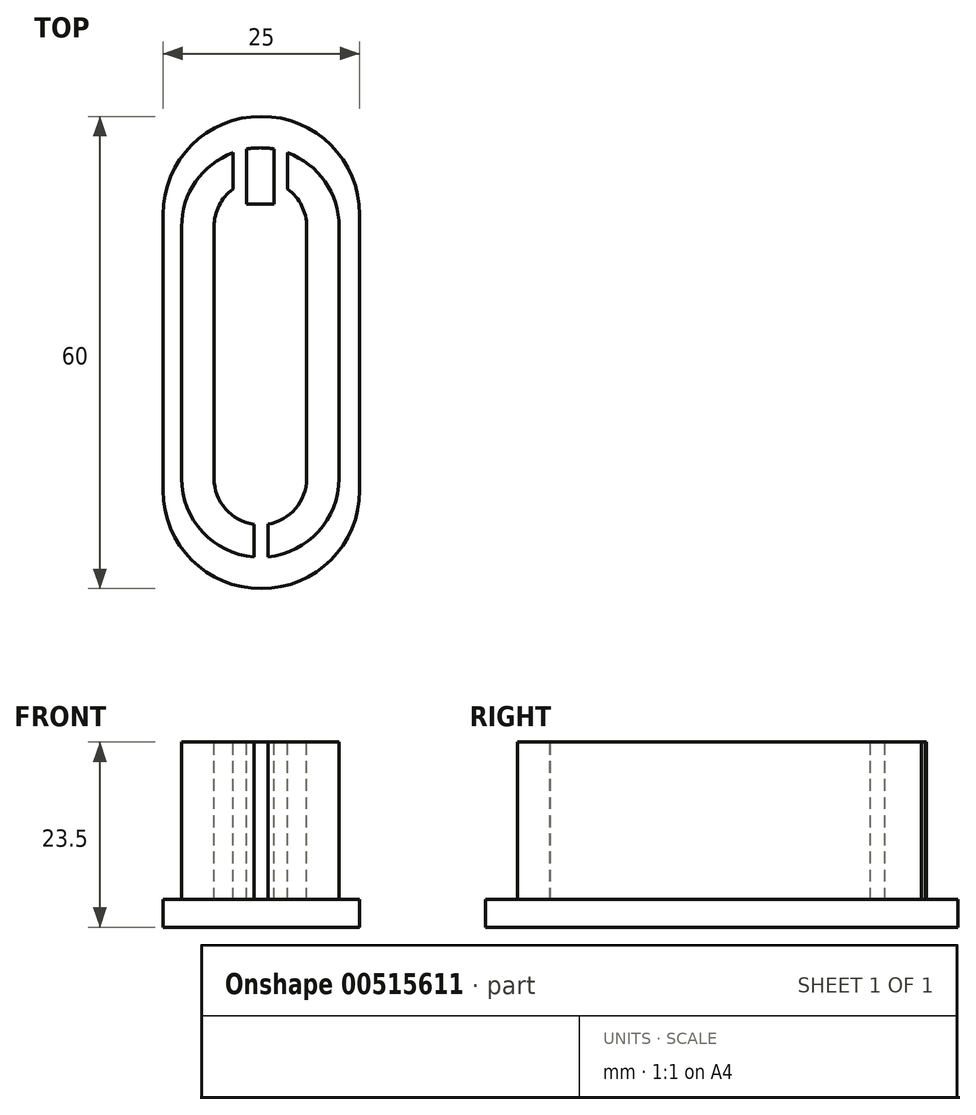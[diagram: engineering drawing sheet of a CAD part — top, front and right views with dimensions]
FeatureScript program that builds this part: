
annotation { "Feature Type Name" : "Feature", "Feature Type Description" : "" }
export const myFeature = defineFeature(function(context is Context, id is Id, definition is map)
    precondition{}
    {
        {
            var Q0;
            Q0=qCreatedBy(makeId("Top.planeOp"),FACE);
            var sketch = newSketch(context, id + "F0", { "sketchPlane" : qUnion([Q0])});
            skLineSegment(sketch, "E0", {"start": v(-12.5, 20) * mm, "end": v(-12.5, -15) * mm});
            skLineSegment(sketch, "E1", {"start": v(12.5, 20) * mm, "end": v(12.5, -15) * mm});
            skArc(sketch, "E2", {"start": v(12.5, 20) * mm, "mid": v(0, 32.5) * mm, "end": v(-12.5, 20) * mm});
            skArc(sketch, "E3", {"start": v(-12.5, -15) * mm, "mid": v(0, -27.5) * mm, "end": v(12.5, -15) * mm});
            skSolve(sketch);
        }
        {
            var Q0;
            Q0 = qSketchRegion(id + "F0", true);
            extrude(context, id + "F1", {"entities" : qUnion([Q0]), "depth" : 3.5 * mm, "offsetDistance" : 25 * mm});
        }
        {
            var Q0;
            Q0=makeQuery(id+"F1.opExtrude","CAP_FACE",FACE,{"disambiguationData":[OSD([sQuery(id+"F0.wireOp",EDGE,"E0"),sQuery(id+"F0.wireOp",EDGE,"E1"),sQuery(id+"F0.wireOp",EDGE,"E2"),sQuery(id+"F0.wireOp",EDGE,"E3")])],"isStart":false});
            var sketch = newSketch(context, id + "F2", { "sketchPlane" : qUnion([Q0])});
            skLineSegment(sketch, "E4.left", {"start": v(-10.13, 18.5) * mm, "end": v(-10.13, -13.5) * mm});
            skLineSegment(sketch, "E4.right", {"start": v(9.87, 18.5) * mm, "end": v(9.87, -13.5) * mm});
            skArc(sketch, "E5", {"start": v(-10.13, -13.5) * mm, "mid": v(-0.13, -23.5) * mm, "end": v(9.87, -13.5) * mm});
            skArc(sketch, "E6", {"start": v(9.87, 18.5) * mm, "mid": v(-0.13, 28.5) * mm, "end": v(-10.13, 18.5) * mm});
            skSolve(sketch);
        }
        {
            var Q0;
            Q0 = qSketchRegion(id + "F2", true);
            extrude(context, id + "F3", {"entities" : qUnion([Q0]), "operationType" : NewBodyOperationType.ADD, "depth" : 20 * mm, "offsetDistance" : 25 * mm});
        }
        {
            var Q0;
            Q0=makeQuery(id+"F3.opExtrude","CAP_FACE",FACE,{"disambiguationData":[OSD([sQuery(id+"F2.wireOp",EDGE,"E4.left"),sQuery(id+"F2.wireOp",EDGE,"E4.right"),sQuery(id+"F2.wireOp",EDGE,"E5"),sQuery(id+"F2.wireOp",EDGE,"E6")])],"isStart":false});
            var sketch = newSketch(context, id + "F4", { "sketchPlane" : qUnion([Q0])});
            skLineSegment(sketch, "E7.left", {"start": v(-6, 18.5) * mm, "end": v(-6, -13.5) * mm});
            skLineSegment(sketch, "E7.right", {"start": v(5.75, 18.5) * mm, "end": v(5.75, -13.5) * mm});
            skArc(sketch, "E8", {"start": v(5.75, 18.5) * mm, "mid": v(5.12, 21.16) * mm, "end": v(3.35, 23.24) * mm});
            skArc(sketch, "E9", {"start": v(-6, -13.5) * mm, "mid": v(-4.55, -17.37) * mm, "end": v(-0.9, -19.33) * mm});
            skLineSegment(sketch, "E10", {"start": v(-3.6, 23.24) * mm, "end": v(-3.6, 27.88) * mm});
            skLineSegment(sketch, "E11", {"start": v(-1.88, 16.66) * mm, "end": v(-1.88, 28.35) * mm});
            skLineSegment(sketch, "E12", {"start": v(1.62, 16.66) * mm, "end": v(1.62, 28.35) * mm});
            skLineSegment(sketch, "E13", {"start": v(3.35, 23.24) * mm, "end": v(3.35, 27.88) * mm});
            skArc(sketch, "E14.trimOffspring", {"start": v(-3.6, 23.24) * mm, "mid": v(-5.37, 21.16) * mm, "end": v(-6, 18.5) * mm});
            skArc(sketch, "E15", {"start": v(-1.88, 28.35) * mm, "mid": v(-2.82, 28.38) * mm, "end": v(-3.6, 27.88) * mm});
            skArc(sketch, "E16", {"start": v(3.35, 27.88) * mm, "mid": v(2.58, 28.47) * mm, "end": v(1.62, 28.35) * mm});
            skLineSegment(sketch, "E17", {"start": v(-0.9, -19.33) * mm, "end": v(-0.9, -23.47) * mm});
            skLineSegment(sketch, "E18", {"start": v(0.82, -19.3) * mm, "end": v(0.82, -23.45) * mm});
            skArc(sketch, "E19.trimOffspring", {"start": v(0.82, -19.3) * mm, "mid": v(4.35, -17.3) * mm, "end": v(5.75, -13.5) * mm});
            skArc(sketch, "E20", {"start": v(-0.9, -23.47) * mm, "mid": v(-0.04, -24.32) * mm, "end": v(0.82, -23.45) * mm});
            skLineSegment(sketch, "E21.top", {"start": v(-1.88, 21.35) * mm, "end": v(1.62, 21.35) * mm});
            skLineSegment(sketch, "E21.left", {"start": v(-1.88, 21.35) * mm, "end": v(-1.88, 16.66) * mm});
            skLineSegment(sketch, "E21.right", {"start": v(1.62, 21.35) * mm, "end": v(1.62, 16.66) * mm});
            skSolve(sketch);
        }
        {
            var Q0;
            Q0 = qSketchRegion(id + "F4", true);
            extrude(context, id + "F5", {"entities" : qUnion([Q0]), "operationType" : NewBodyOperationType.REMOVE, "oppositeDirection" : true, "depth" : 20 * mm, "offsetDistance" : 25 * mm});
        }
    });
